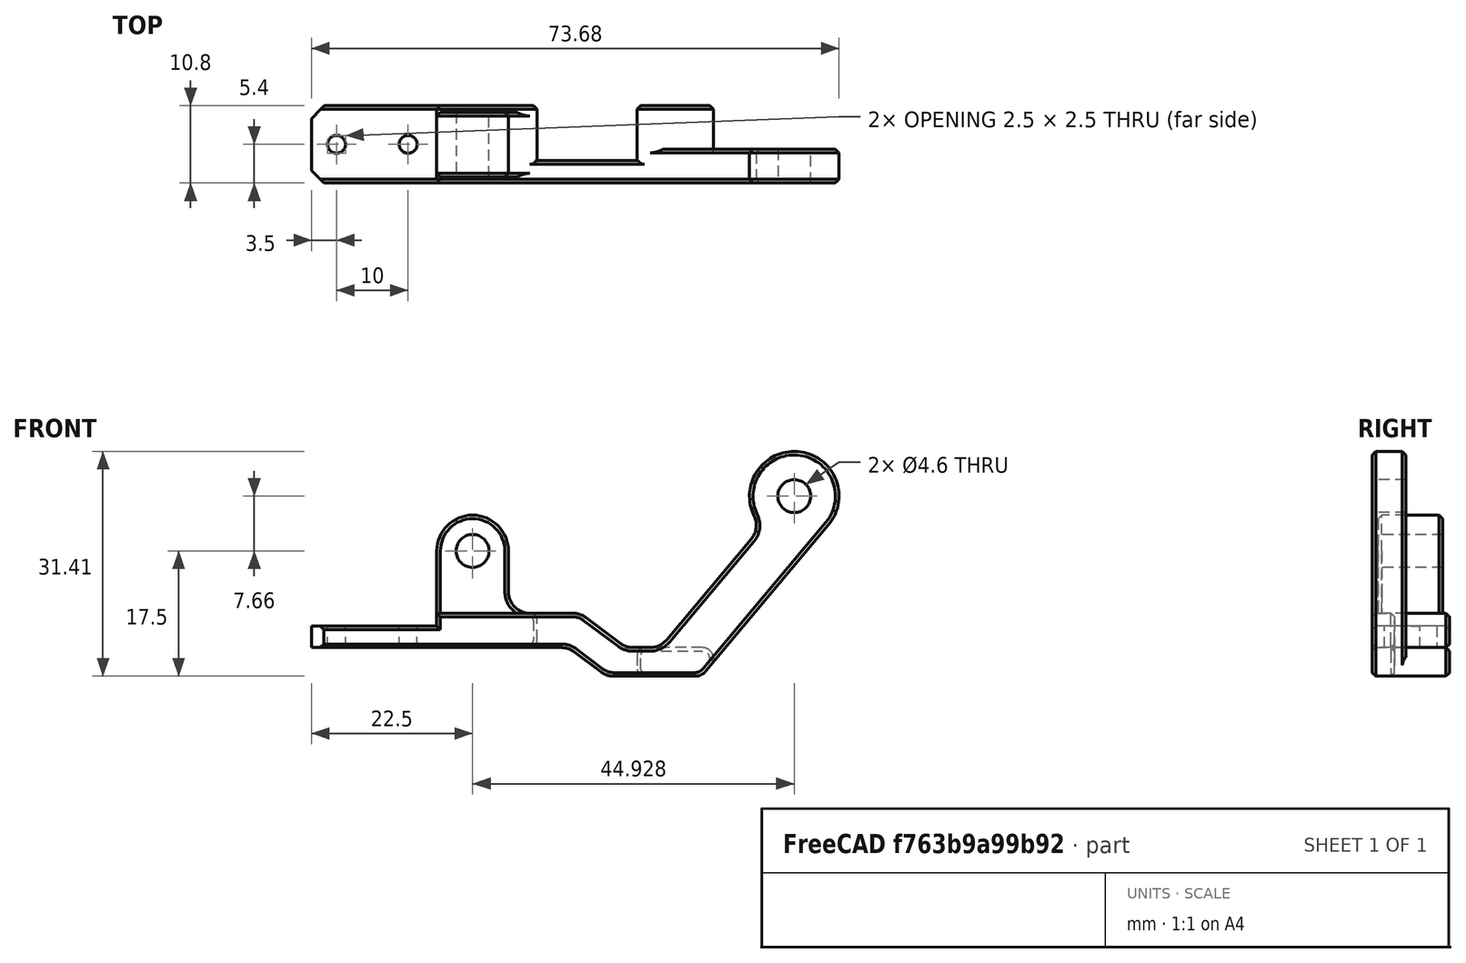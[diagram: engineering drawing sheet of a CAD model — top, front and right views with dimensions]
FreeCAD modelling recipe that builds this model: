
FCSTD DOCUMENT  (FreeCAD 0.18R16146 (Git))
Label: WIPOddShapedPart
License: All rights reserved
LicenseURL: http://en.wikipedia.org/wiki/All_rights_reserved
objects: Part::Feature×1, PartDesign::FeatureBase×1, Sketcher::SketchObject×1, PartDesign::Pocket×1, PartDesign::Body×1
note: 6 computed .brp shape members not serialized (recipe doc carries the construction recipe); baked Part::Feature solids carry a one-line shape summary decoded from their .brp

FEATURE [Part::Feature] Part__Feature015  label="½Á´"
  Placement = pos=(106.263,283.627,-119.954) rot=(0.948592,0.2238,0.2238;1.62355rad)
  shape: bbox 76.03 x 34.74 x 10.8 mm, 107 faces (baked)
FEATURE [PartDesign::FeatureBase] BaseFeature
  BaseFeature = -> Part__Feature015
FEATURE [Sketcher::SketchObject] Sketch
  ExternalGeometry = -> [BaseFeature]
  MapMode = 5
  Placement = pos=(8e-16,-5.4,0) rot=(1,0,0;1.5708rad)
  Support = -> [BaseFeature]
  sketch-geometry (2):
    g0: Circle CenterX=0 CenterY=12.5 CenterZ=0 NormalX=0 NormalY=0 NormalZ=1 AngleXU=0 Radius=2.3
    g1: Circle CenterX=44.9279 CenterY=20.1604 CenterZ=0 NormalX=0 NormalY=0 NormalZ=1 AngleXU=0 Radius=2.3
  constraints (4):
    c: Coincident(g0,g-4)
    c: Radius(g0) = 2.3
    c: Coincident(g1,g-6)
    c: Radius(g1) = 2.3
FEATURE [PartDesign::Pocket] Pocket
  BaseFeature = -> BaseFeature
  Length = 5
  Length2 = 100
  Profile = -> Sketch
  Type = 1
FEATURE [PartDesign::Body] Body
  BaseFeature = -> Part__Feature015
  Group = -> [BaseFeature,Sketch,Pocket]
  Origin = -> Origin
  Tip = -> Pocket
